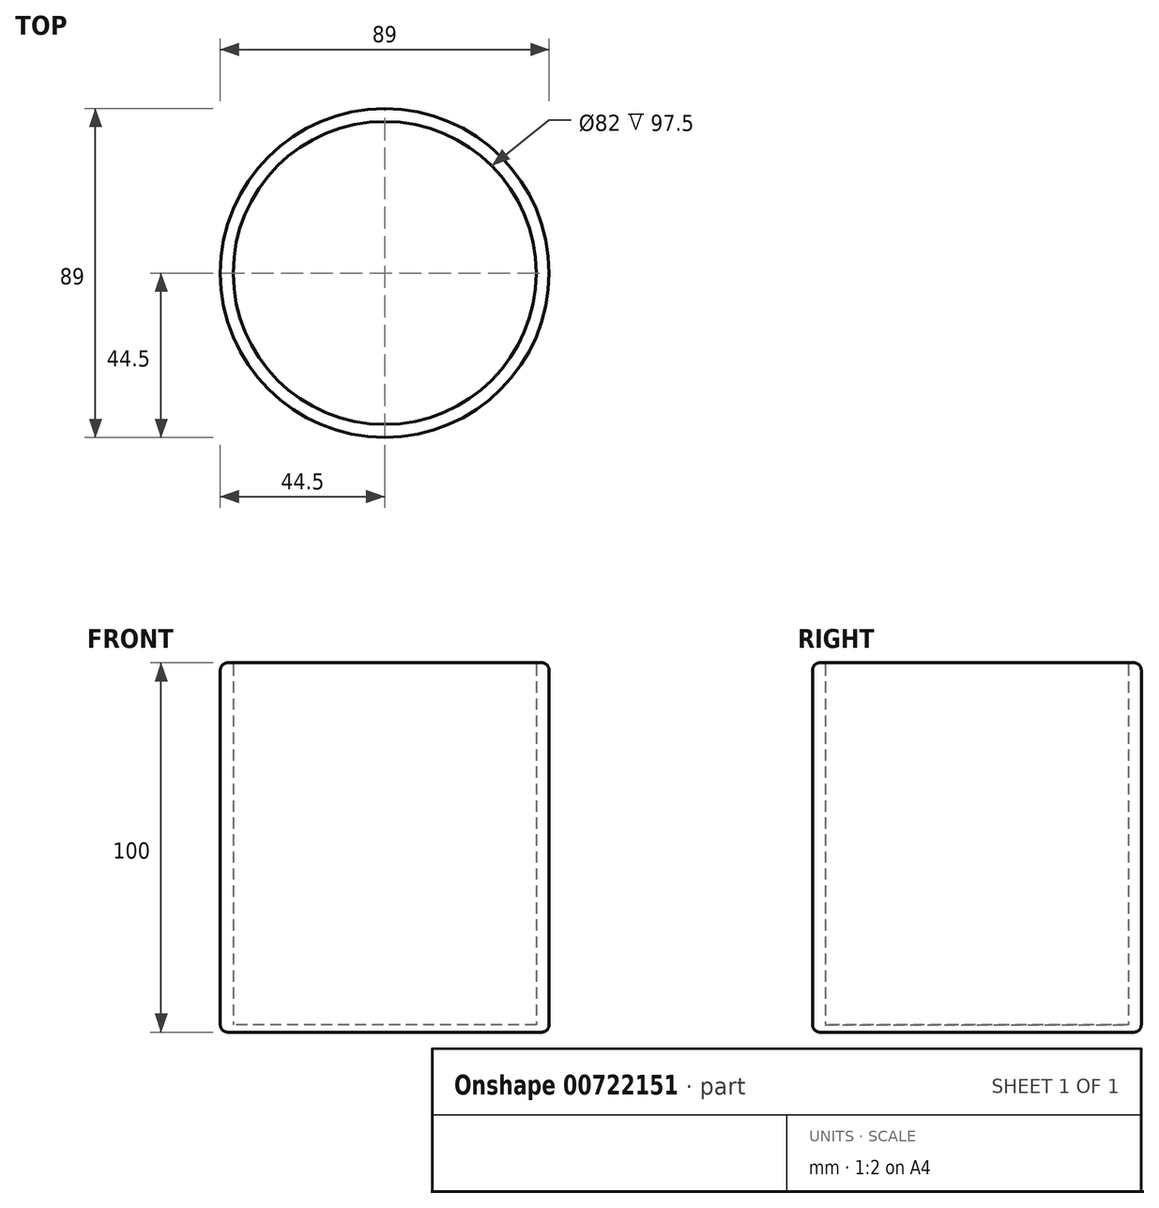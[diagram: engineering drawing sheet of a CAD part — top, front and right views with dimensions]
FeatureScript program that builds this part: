
annotation { "Feature Type Name" : "Feature", "Feature Type Description" : "" }
export const myFeature = defineFeature(function(context is Context, id is Id, definition is map)
    precondition{}
    {
        {
            var Q0;
            Q0=qCreatedBy(makeId("Top.planeOp"),FACE);
            var sketch = newSketch(context, id + "F0", { "sketchPlane" : qUnion([Q0])});
            skCircle(sketch, "E0", {"center": v(0, 0) * mm, "radius": 44.5 * mm});
            skCircle(sketch, "E1", {"center": v(0, 0) * mm, "radius": 41 * mm});
            skSolve(sketch);
        }
        {
            var Q0;
            Q0=makeQuery(id+"F0.imprint","IMPRINT",FACE,{"disambiguationData":[TD([[makeQuery(id+"F0.imprint","IMPRINT",EDGE,{"derivedFrom":sQuery(id+"F0.wireOp",EDGE,"E0")}),1.0]])]});
            extrude(context, id + "F1", {"entities" : qUnion([Q0]), "depth" : 100 * mm, "offsetDistance" : 25.4 * mm});
        }
        {
            var Q0;
            Q0=makeQuery(id+"F1.opExtrude","CAP_EDGE",EDGE,{"disambiguationData":[OSD([sQuery(id+"F0.wireOp",EDGE,"E0")])],"isStart":false});
            var Q1;
            Q1=makeQuery(id+"F1.opExtrude","CAP_EDGE",EDGE,{"disambiguationData":[OSD([sQuery(id+"F0.wireOp",EDGE,"E0")])],"isStart":true});
            fillet(context, id + "F2", {"entities" : qUnion([Q0, Q1]), "radius" : 2 * mm, "tangentPropagation" : true, "allowEdgeOverflow" : false});
        }
        {
            var Q0;
            Q0=makeQuery(id+"F1.opExtrude","CAP_EDGE",EDGE,{"disambiguationData":[OSD([sQuery(id+"F0.wireOp",EDGE,"E1")])],"isStart":false});
            fillet(context, id + "F3", {"entities" : qUnion([Q0]), "radius" : .5 * mm, "tangentPropagation" : true, "allowEdgeOverflow" : false});
        }
        {
            var Q0;
            Q0=makeQuery(id+"F0.imprint","IMPRINT",FACE,{"disambiguationData":[TD([[makeQuery(id+"F0.imprint","IMPRINT",EDGE,{"derivedFrom":sQuery(id+"F0.wireOp",EDGE,"E1")}),1.0]])]});
            extrude(context, id + "F4", {"entities" : qUnion([Q0]), "operationType" : NewBodyOperationType.ADD, "depth" : 2 * mm, "offsetDistance" : 25.4 * mm});
        }
    });
